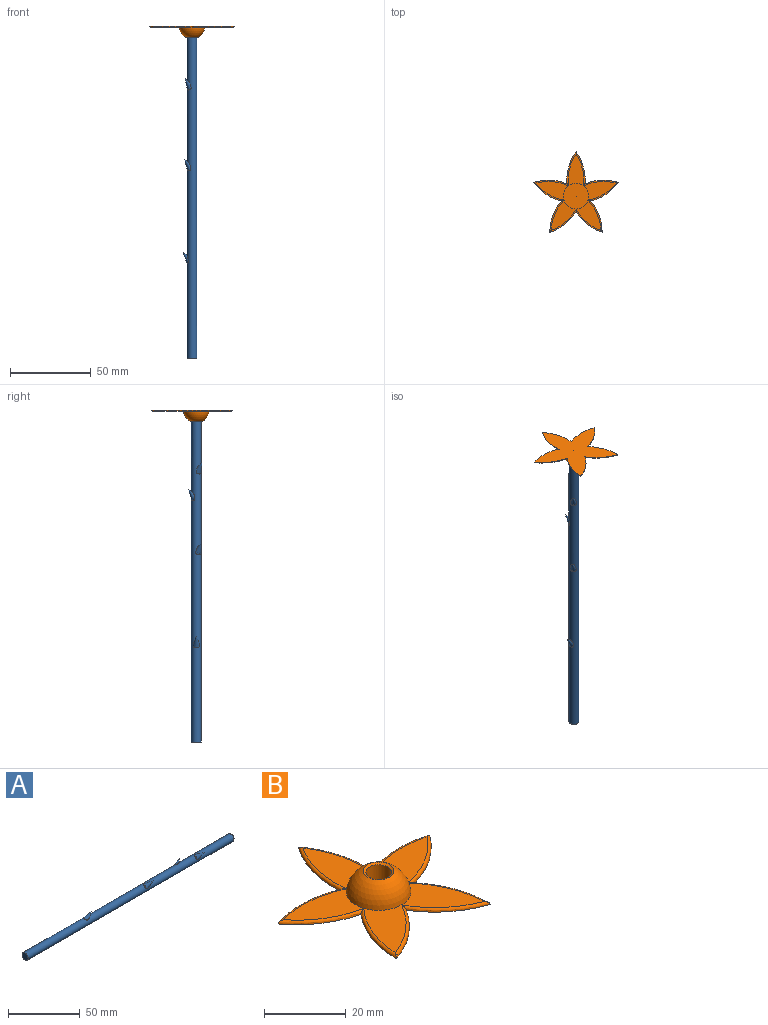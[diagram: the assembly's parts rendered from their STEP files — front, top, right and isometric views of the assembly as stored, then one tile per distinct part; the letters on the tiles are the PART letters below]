
ASSEMBLY  parts=2 mates=1
PART A: 17 faces, bbox 203.2x8.2x8.6 mm
  f0: cylinder r=3mm len=202.57mm, axis (-1,0,0), area 3588.6mm2, adj f1,f2,f3,f4,f5,f6,f8,f9
  f1: cone r=2.38mm half-angle=18.7deg, axis (-0.78,0.4,-0.48), area 31.2mm2, adj f0,f2
  f2: cone r=2.38mm half-angle=38.7deg, axis (-0.78,0.4,-0.48), area 0.3mm2, adj f0,f1
  f3: cone r=0mm half-angle=38.7deg, axis (-0.78,-0.53,-0.34), area 0.4mm2, adj f0,f4
  f4: cone r=2.38mm half-angle=18.7deg, axis (-0.78,-0.53,-0.34), area 31.4mm2, adj f0,f3
  f5: cone r=2.64mm half-angle=18.7deg, axis (-0.78,0,-0.63), area 30.8mm2, adj f0
  f6: plane 6x6mm, normal (-1,0,0), area 28.3mm2, adj f0,f7,f8,f12
  f7: plane 202.44x0.8mm, normal (0,0,-1), area 162mm2, adj f6,f8,f11,f12
  f8: plane 202.46x0.03mm, normal (0,1,0), area 5.4mm2, adj f0,f6,f7,f11
  f9: cone r=2.36mm half-angle=45deg, axis (-1,0,0), area 13.6mm2, adj f0,f10,f11
  f10: plane 4.73x4.6mm, normal (1,0,0), area 17.4mm2, adj f9,f11
  f11: plane 1.75x0.78mm, normal (0.71,0,-0.71), area 1.7mm2, adj f0,f7,f8,f9,f10,f12
  f12: plane 202.46x0.03mm, normal (0,-1,0), area 5.4mm2, adj f0,f6,f7,f11
  f13: cone r=0mm half-angle=38.7deg, axis (-0.78,0.36,-0.51), area 0mm2, adj f0
  f14: cone r=0mm half-angle=38.7deg, axis (-0.78,0.36,-0.51), area 0mm2, adj f0
  f15: cone r=0mm half-angle=38.7deg, axis (-0.78,0.36,-0.51), area 0.3mm2, adj f0,f16
  f16: cone r=2.38mm half-angle=18.7deg, axis (-0.78,0.36,-0.51), area 31.2mm2, adj f0,f15
PART B: 16 faces, bbox 56.3x53.6x7 mm
  f0: sphere r=7.94mm, area 308.8mm2, adj f1,f5
  f1: plane 49.69x47.25mm, normal (0,0,1), area 659.7mm2, adj f0,f6,f7,f8,f9,f10,f11,f12
  f2: plane 52.36x49.79mm, normal (0,0,-1), area 1022.3mm2, adj f6,f7,f8,f9,f10,f11,f12,f13
  f3: cone r=0mm half-angle=59deg, axis (0,0,1), area 36.1mm2, adj f4
  f4: cylinder r=3.14mm len=6.28mm, axis (0,0,1), area 89.4mm2, adj f3,f5
  f5: cone r=3.76mm half-angle=59.1deg, axis (0,0,1), area 15.5mm2, adj f0,f4
  f6: torus R=29.2mm, axis (0,0,1), area 26.3mm2, adj f1,f2,f7,f8
  f7: torus R=29.2mm, axis (0,0,1), area 26.3mm2, adj f1,f2,f6,f9
  f8: torus R=29.2mm, axis (0,0,1), area 26.3mm2, adj f1,f2,f6,f10
  f9: torus R=29.2mm, axis (0,0,1), area 26.3mm2, adj f1,f2,f7,f11
  f10: torus R=29.2mm, axis (0,0,1), area 26.3mm2, adj f1,f2,f8,f12
  f11: torus R=29.2mm, axis (0,0,1), area 26.3mm2, adj f1,f2,f9,f13
  f12: torus R=29.2mm, axis (0,0,1), area 26.3mm2, adj f1,f2,f10,f14
  f13: torus R=29.2mm, axis (0,0,1), area 26.3mm2, adj f1,f2,f11,f15
  f14: torus R=29.2mm, axis (0,0,1), area 26.3mm2, adj f1,f2,f12,f15
  f15: torus R=29.2mm, axis (0,0,1), area 26.3mm2, adj f1,f2,f13,f14
PLACE A rot(axis=(0,-1,0),90deg) t=(3.16,-0.93,-13.25)mm
PLACE B rot(axis=(0,1,0),180deg) t=(0.16,-0.93,90.44)mm
MATE fastened B.f3 <-> A.f0  axis (0,0,-1) through (0.16,-0.93,88.35)mm
